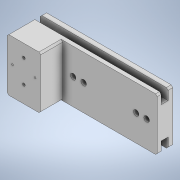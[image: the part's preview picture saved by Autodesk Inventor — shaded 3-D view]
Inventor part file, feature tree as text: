
AUTODESK INVENTOR PART (.ipt)
format: ipt  version: 2020 (Build 240168000, 168)  size: 217,600 bytes
history: native  units: in
note: dims shown in document units (in); Inventor stores cm internally (conversion verified against a paired STEP export)
features: sketch x6, extrude x4, hole x3, chamfer x2
ambient origin geometry x8: Origin, YZ Plane, XZ Plane, XY Plane, X Axis, Y Axis, Z Axis, Center Point
bodies: Solid1 (feature_tree)
feature tree (15):
  extrude  "Extrusion1"  Depth=2.5in
  extrude  "Extrusion2"  Depth=0.7441in
  hole  "Hole2"  [1 undecoded]
  sketch  "Sketch4"  dims[d7=1.0535in d8=0.0in]
  extrude  "Extrusion3"  TaperAngle=0.0deg  [1 undecoded]
  extrude  "Extrusion4"  TaperAngle=0.0deg  [1 undecoded]
  sketch  "Sketch6"  dims[d11=0.0in d12=0.0in d13=3.5in d14=0.5in d15=2.5in d16=0.5in d24=0.2638in d25=0.7874in d26=0.4331in d27=0.252in d28=90.0deg d29=0.7087in d30=0.0in d31=6.0925in d32=3.0463in d33=0.3917in d35=0.3287in d36=6.0925in d37=0.0in d38=0.3917in d40=0.0in d41=0.5in d42=0.0in d43=0.0in d44=0.5965in d45=0.0in d46=0.7972in d47=0.7963in d48=1.1063in d50=1.0748in d51=0.5531in d52=0.5374in d53=0.0827in d54=0.2362in d55=0.1575in d56=0.0787in d57=90.0deg d58=0.1614in d59=0.0in d60=0.13in d61=0.328in d62=0.3319in d63=0.0787in d64=0.5635in d65=0.4843in d66=0.0in d67=0.0413in d68=0.0394in d69=0.0394in d70=0.0787in d71=45.0deg d72=0.0787in d73=0.0787in d74=45.0deg d75=0.5635in d76=0.0295in d77=0.8108in d78=0.0025in d79=0.0295in d80=0.0148in]
  hole  "Hole3"  [1 undecoded]
  hole  "Hole4"  [1 undecoded]
  chamfer  "Chamfer1"  Distance=0.5in
  chamfer  "Chamfer2"  Distance=2.5in
  sketch  "Sketch1"  dims[d0=2.5in d1=1.25in]
  sketch  "Sketch2"  dims[d2=1.5925in d4=0.7441in]
  sketch  "Sketch3"  dims[d5=0.0in d6=1.5925in]
  sketch  "Sketch5"  dims[d9=0.0in d10=0.0in]
note: 5 required parameter values undecoded (feature->parameter linkage not recoverable at this tier; creation-order binding heuristic only, values carry confidence <= 0.55)
